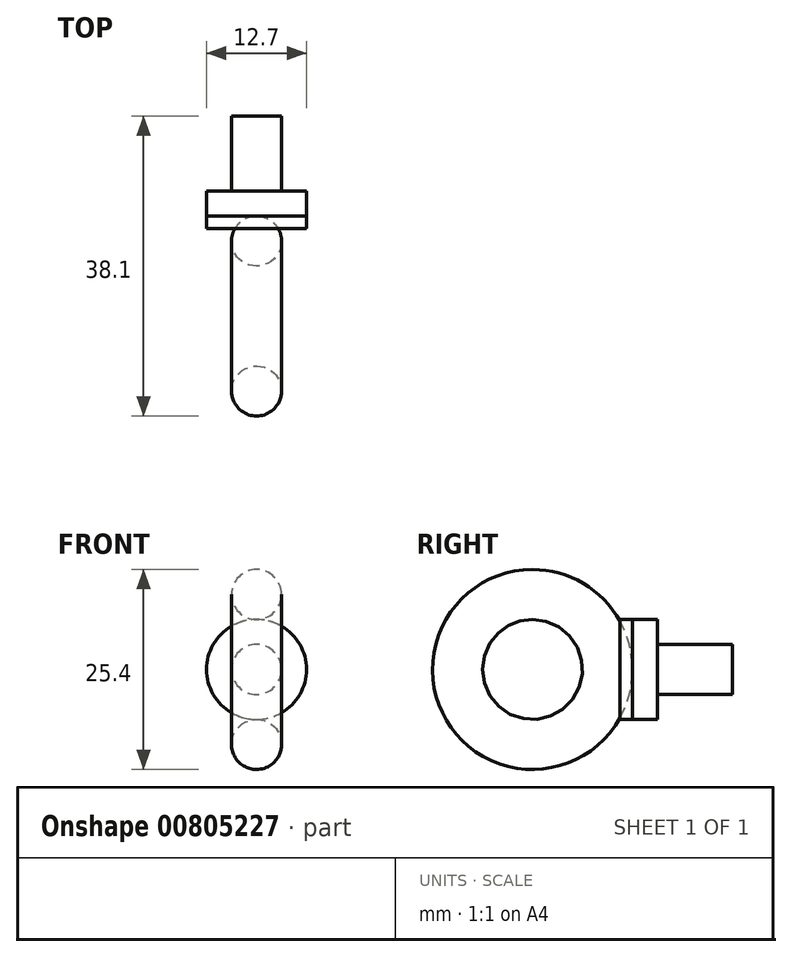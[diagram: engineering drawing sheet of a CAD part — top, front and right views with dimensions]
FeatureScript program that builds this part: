
annotation { "Feature Type Name" : "Feature", "Feature Type Description" : "" }
export const myFeature = defineFeature(function(context is Context, id is Id, definition is map)
    precondition{}
    {
        {
            var Q0;
            Q0=qCreatedBy(makeId("Front.planeOp"),FACE);
            cPlane(context, id + "F0", {"entities" : qUnion([Q0]), "cplaneType" : CPlaneType.OFFSET, "offset" : 12.7 * mm, "oppositeDirection" : true, "width" : 152.4 * mm, "height" : 152.4 * mm});
        }
        {
            var Q0;
            Q0=qCreatedBy(makeId("Top.planeOp"),FACE);
            var sketch = newSketch(context, id + "F1", { "sketchPlane" : qUnion([Q0])});
            skLineSegment(sketch, "E0", {"start": v(-18.84, 0) * mm, "end": v(27.05, 0) * mm, "construction": true});
            skSolve(sketch);
        }
        {
            var Q0;
            Q0=qCreatedBy(id+"F0.planeOp",FACE);
            var sketch = newSketch(context, id + "F2", { "sketchPlane" : qUnion([Q0])});
            skCircle(sketch, "E1", {"center": v(0, 0) * mm, "radius": 6.35 * mm});
            skSolve(sketch);
        }
        {
            var Q0;
            Q0=makeQuery(id+"F2.imprint","IMPRINT",FACE,{"disambiguationData":[TD([[makeQuery(id+"F2.imprint","IMPRINT",EDGE,{"derivedFrom":sQuery(id+"F2.wireOp",EDGE,"E1")}),1.0]])]});
            extrude(context, id + "F3", {"entities" : qUnion([Q0]), "oppositeDirection" : true, "depth" : 3.17 * mm, "offsetDistance" : 25.4 * mm});
        }
        {
            var Q0;
            Q0=makeQuery(id+"F3.opExtrude","CAP_FACE",FACE,{"disambiguationData":[OSD([sQuery(id+"F2.wireOp",EDGE,"E1")])],"isStart":false});
            var sketch = newSketch(context, id + "F4", { "sketchPlane" : qUnion([Q0])});
            skCircle(sketch, "E2", {"center": v(0, 0) * mm, "radius": 3.18 * mm});
            skSolve(sketch);
        }
        {
            var Q0;
            Q0 = qSketchRegion(id + "F4", true);
            extrude(context, id + "F5", {"entities" : qUnion([Q0]), "operationType" : NewBodyOperationType.ADD, "depth" : 9.52 * mm, "offsetDistance" : 25.4 * mm});
        }
        {
            var Q0;
            Q0=qCreatedBy(makeId("Top.planeOp"),FACE);
            var sketch = newSketch(context, id + "F6", { "sketchPlane" : qUnion([Q0])});
            skLineSegment(sketch, "E3.0", {"start": v(6.35, 12.7) * mm, "end": v(-6.35, 12.7) * mm, "construction": true});
            skCircle(sketch, "E4", {"center": v(0, 9.53) * mm, "radius": 3.18 * mm});
            skPoint(sketch, "E4.centerSnap0", {"position": v(0, 12.7) * mm});
            skSolve(sketch);
        }
        {
            var Q0;
            Q0=makeQuery(id+"F6.imprint","IMPRINT",FACE,{"disambiguationData":[TD([[makeQuery(id+"F6.imprint","IMPRINT",EDGE,{"derivedFrom":sQuery(id+"F6.wireOp",EDGE,"E4")}),1.0]])]});
            var Q1;
            Q1=sQuery(id+"F1.wireOp",EDGE,"E0");
            revolve(context, id + "F7", {"surfaceOperationType" : NewSurfaceOperationType.NEW, "entities" : qUnion([Q0]), "axis" : qUnion([Q1]), "revolveType" : RevolveType.FULL});
        }
        {
            var Q0;
            Q0=makeQuery(id+"F3.opExtrude","CAP_FACE",FACE,{"disambiguationData":[OSD([sQuery(id+"F2.wireOp",EDGE,"E1")])],"isStart":true});
            extrude(context, id + "F8", {"entities" : qUnion([Q0]), "depth" : 1.59 * mm, "offsetDistance" : 25.4 * mm});
        }
    });
